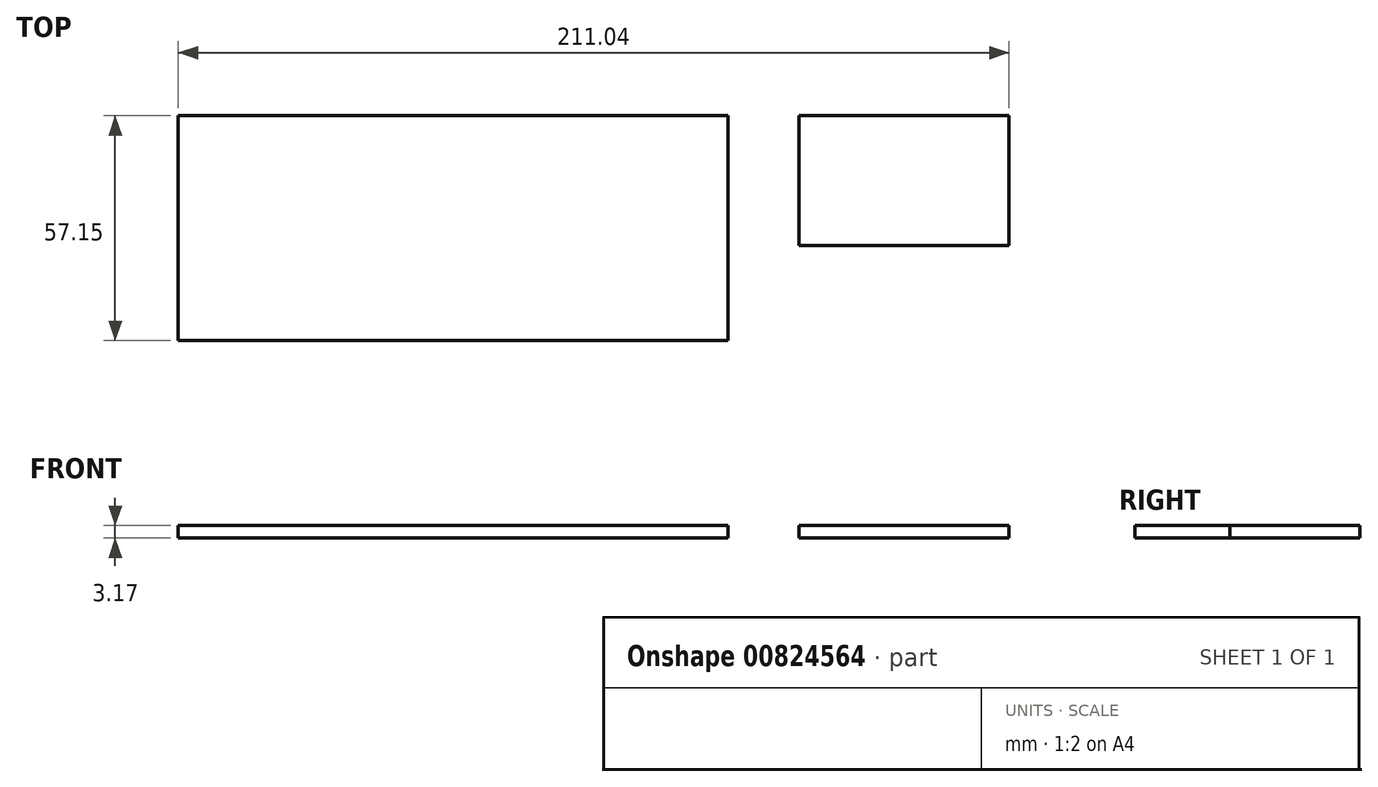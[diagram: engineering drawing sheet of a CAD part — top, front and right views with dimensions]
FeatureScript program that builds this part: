
annotation { "Feature Type Name" : "Feature", "Feature Type Description" : "" }
export const myFeature = defineFeature(function(context is Context, id is Id, definition is map)
    precondition{}
    {
        {
            var Q0;
            Q0=qCreatedBy(makeId("Top.planeOp"),FACE);
            var sketch = newSketch(context, id + "F0", { "sketchPlane" : qUnion([Q0])});
            skLineSegment(sketch, "E0.bottom", {"start": v(-96.73, 57.15) * mm, "end": v(-82.76, 57.15) * mm});
            skLineSegment(sketch, "E0.top", {"start": v(-96.73, 0) * mm, "end": v(-82.76, 0) * mm});
            skLineSegment(sketch, "E0.left", {"start": v(-96.73, 57.15) * mm, "end": v(-96.73, 0) * mm});
            skLineSegment(sketch, "E0.right", {"start": v(-82.76, 57.15) * mm, "end": v(-82.76, 0) * mm});
            skLineSegment(sketch, "E1.bottom", {"start": v(-82.76, 57.15) * mm, "end": v(-68.8, 57.15) * mm});
            skLineSegment(sketch, "E1.top", {"start": v(-82.76, 0) * mm, "end": v(-68.8, 0) * mm});
            skLineSegment(sketch, "E1.right", {"start": v(-68.8, 57.15) * mm, "end": v(-68.8, 0) * mm});
            skLineSegment(sketch, "E2.bottom", {"start": v(-68.8, 57.15) * mm, "end": v(-54.82, 57.15) * mm});
            skLineSegment(sketch, "E2.top", {"start": v(-68.8, 0) * mm, "end": v(-54.82, 0) * mm});
            skLineSegment(sketch, "E2.right", {"start": v(-54.82, 57.15) * mm, "end": v(-54.82, 0) * mm});
            skLineSegment(sketch, "E3.bottom", {"start": v(-54.82, 57.15) * mm, "end": v(-40.85, 57.15) * mm});
            skLineSegment(sketch, "E3.top", {"start": v(-54.82, 0) * mm, "end": v(-40.85, 0) * mm});
            skLineSegment(sketch, "E4.bottom", {"start": v(-40.85, 57.15) * mm, "end": v(-26.88, 57.15) * mm});
            skLineSegment(sketch, "E4.top", {"start": v(-40.85, 0) * mm, "end": v(-26.88, 0) * mm});
            skLineSegment(sketch, "E4.left", {"start": v(-40.85, 57.15) * mm, "end": v(-40.85, 0) * mm});
            skLineSegment(sketch, "E4.right", {"start": v(-26.88, 57.15) * mm, "end": v(-26.88, 0) * mm});
            skLineSegment(sketch, "E5.bottom", {"start": v(-26.88, 57.15) * mm, "end": v(-12.91, 57.15) * mm});
            skLineSegment(sketch, "E5.top", {"start": v(-26.88, 0) * mm, "end": v(-12.91, 0) * mm});
            skLineSegment(sketch, "E5.right", {"start": v(-12.91, 57.15) * mm, "end": v(-12.91, 0) * mm});
            skLineSegment(sketch, "E6.bottom", {"start": v(29, 57.15) * mm, "end": v(42.97, 57.15) * mm});
            skLineSegment(sketch, "E6.top", {"start": v(29, 0) * mm, "end": v(42.97, 0) * mm});
            skLineSegment(sketch, "E6.right", {"start": v(42.97, 57.15) * mm, "end": v(42.97, 0) * mm});
            skLineSegment(sketch, "E7.bottom", {"start": v(15.03, 57.15) * mm, "end": v(29, 57.15) * mm});
            skLineSegment(sketch, "E7.top", {"start": v(15.03, 0) * mm, "end": v(29, 0) * mm});
            skLineSegment(sketch, "E7.left", {"start": v(15.03, 57.15) * mm, "end": v(15.03, 0) * mm});
            skLineSegment(sketch, "E7.right", {"start": v(29, 57.15) * mm, "end": v(29, 0) * mm});
            skLineSegment(sketch, "E8.bottom", {"start": v(1.06, 57.15) * mm, "end": v(15.03, 57.15) * mm});
            skLineSegment(sketch, "E8.top", {"start": v(1.06, 0) * mm, "end": v(15.03, 0) * mm});
            skLineSegment(sketch, "E8.left", {"start": v(1.06, 57.15) * mm, "end": v(1.06, 0) * mm});
            skLineSegment(sketch, "E9.bottom", {"start": v(-12.91, 57.15) * mm, "end": v(1.06, 57.15) * mm});
            skLineSegment(sketch, "E9.top", {"start": v(-12.91, 0) * mm, "end": v(1.06, 0) * mm});
            skLineSegment(sketch, "E10.bottom", {"start": v(60.96, 57.15) * mm, "end": v(69.86, 57.15) * mm});
            skLineSegment(sketch, "E10.top", {"start": v(60.96, 24.13) * mm, "end": v(69.86, 24.13) * mm});
            skLineSegment(sketch, "E10.left", {"start": v(60.96, 57.15) * mm, "end": v(60.96, 24.13) * mm});
            skPoint(sketch, "E11", {"position": v(8.04, 57.15) * mm});
            skLineSegment(sketch, "E12.bottom", {"start": v(69.86, 57.15) * mm, "end": v(78.75, 57.15) * mm});
            skLineSegment(sketch, "E12.top", {"start": v(69.86, 24.13) * mm, "end": v(78.75, 24.13) * mm});
            skLineSegment(sketch, "E12.left", {"start": v(69.86, 57.15) * mm, "end": v(69.86, 24.13) * mm});
            skLineSegment(sketch, "E13.bottom", {"start": v(78.75, 57.15) * mm, "end": v(87.64, 57.15) * mm});
            skLineSegment(sketch, "E13.top", {"start": v(78.75, 24.13) * mm, "end": v(87.64, 24.13) * mm});
            skLineSegment(sketch, "E13.left", {"start": v(78.75, 57.15) * mm, "end": v(78.75, 24.13) * mm});
            skLineSegment(sketch, "E14.bottom", {"start": v(87.64, 57.15) * mm, "end": v(96.53, 57.15) * mm});
            skLineSegment(sketch, "E14.top", {"start": v(87.64, 24.13) * mm, "end": v(96.53, 24.13) * mm});
            skLineSegment(sketch, "E14.left", {"start": v(87.64, 57.15) * mm, "end": v(87.64, 24.13) * mm});
            skLineSegment(sketch, "E14.right", {"start": v(96.53, 57.15) * mm, "end": v(96.53, 24.13) * mm});
            skLineSegment(sketch, "E15.bottom", {"start": v(96.53, 57.15) * mm, "end": v(105.42, 57.15) * mm});
            skLineSegment(sketch, "E15.top", {"start": v(96.53, 24.13) * mm, "end": v(105.42, 24.13) * mm});
            skLineSegment(sketch, "E15.right", {"start": v(105.42, 57.15) * mm, "end": v(105.42, 24.13) * mm});
            skLineSegment(sketch, "E16.bottom", {"start": v(105.42, 57.15) * mm, "end": v(114.31, 57.15) * mm});
            skLineSegment(sketch, "E16.top", {"start": v(105.42, 24.13) * mm, "end": v(114.31, 24.13) * mm});
            skLineSegment(sketch, "E16.right", {"start": v(114.31, 57.15) * mm, "end": v(114.31, 24.13) * mm});
            skSolve(sketch);
        }
        {
            var Q0;
            Q0 = qSketchRegion(id + "F0", true);
            extrude(context, id + "F1", {"entities" : qUnion([Q0]), "depth" : 3.17 * mm, "offsetDistance" : 25.4 * mm});
        }
        {
            var Q0;
            Q0 = qSketchRegion(id + "F0", true);
            extrude(context, id + "F2", {"entities" : qUnion([Q0]), "depth" : 3.17 * mm, "offsetDistance" : 25.4 * mm});
        }
    });
